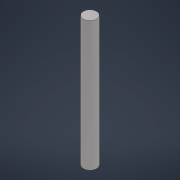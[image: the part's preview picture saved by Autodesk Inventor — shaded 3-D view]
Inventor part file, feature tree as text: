
AUTODESK INVENTOR PART (.ipt)
format: ipt  version: 2021 (Build 250183000, 183)  size: 87,040 bytes
history: native  units: mm
features: other x2, extrude x1, sketch x1
ambient origin geometry x8: Origin, YZ Plane, XZ Plane, XY Plane, X Axis, Y Axis, Z Axis, Center Point
bodies: Body1 (feature_tree)
feature tree (4):
  other  "Eixo Maior - Engrenagem"
  other  "Sólido1"
  extrude  "Extrusão1"  Depth=8.8mm TaperAngle=0.0deg
  sketch  "Esboço1"  dims[d0=0.9mm d1=8.8mm d2=0.0mm]
